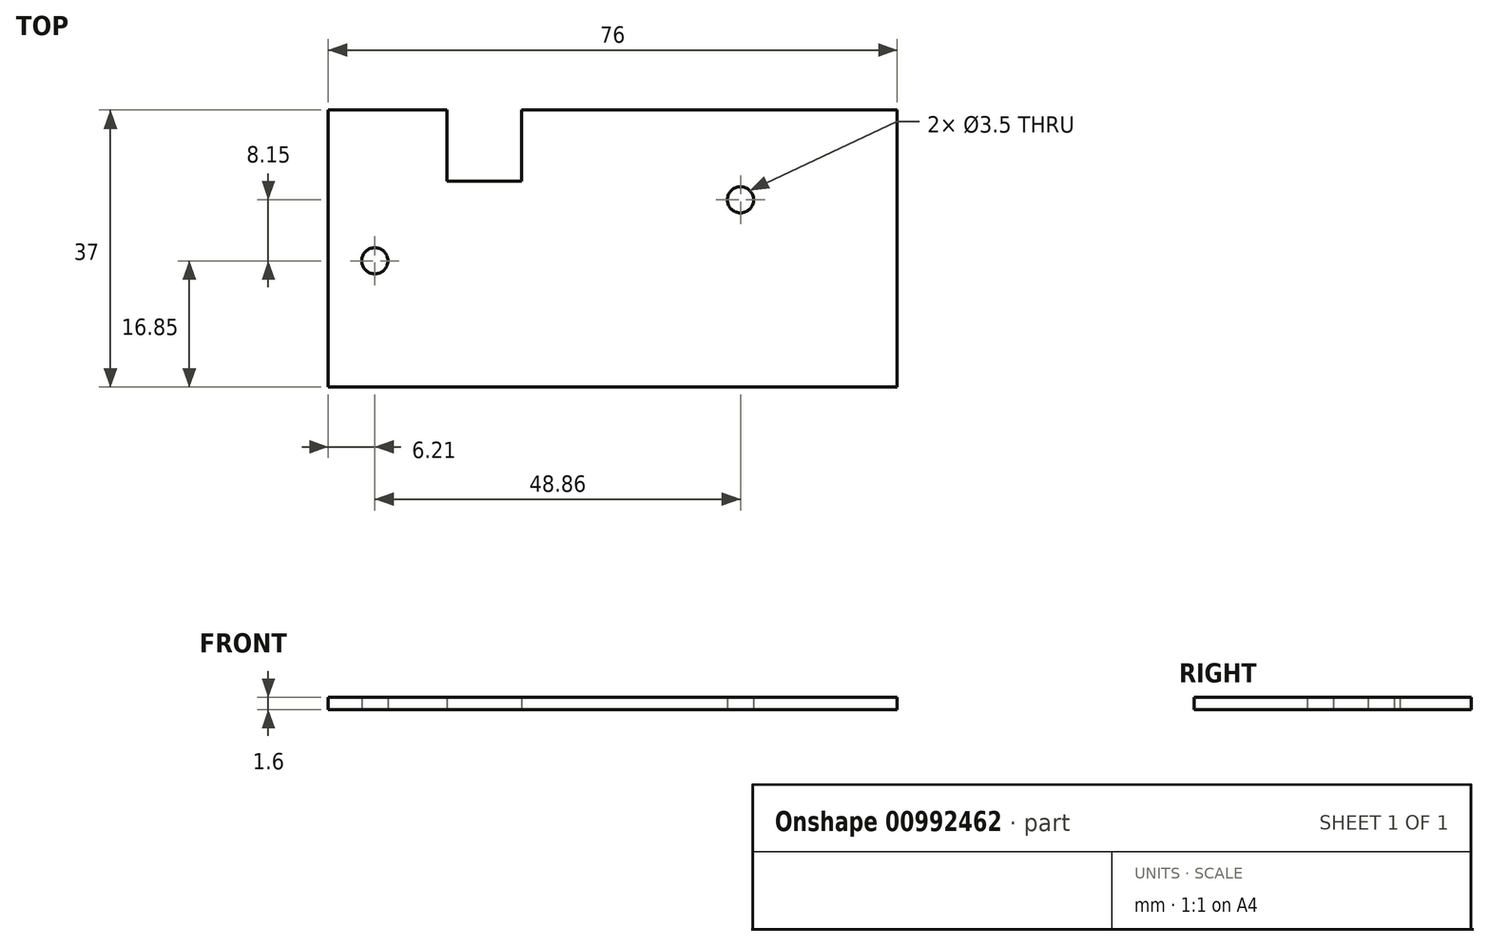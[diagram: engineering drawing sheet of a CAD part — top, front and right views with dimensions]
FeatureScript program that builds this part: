
annotation { "Feature Type Name" : "Feature", "Feature Type Description" : "" }
export const myFeature = defineFeature(function(context is Context, id is Id, definition is map)
    precondition{}
    {
        {
            var Q0;
            Q0=qCreatedBy(makeId("Top.planeOp"),FACE);
            var sketch = newSketch(context, id + "F0", { "sketchPlane" : qUnion([Q0])});
            skLineSegment(sketch, "E0.bottom", {"start": v(-38, 18.5) * mm, "end": v(-22.17, 18.5) * mm});
            skLineSegment(sketch, "E0.top", {"start": v(-38, -18.5) * mm, "end": v(38, -18.5) * mm});
            skLineSegment(sketch, "E0.left", {"start": v(-38, 18.5) * mm, "end": v(-38, -18.5) * mm});
            skLineSegment(sketch, "E0.right", {"start": v(38, 18.5) * mm, "end": v(38, -18.5) * mm});
            skLineSegment(sketch, "E1.top", {"start": v(-22.17, 9) * mm, "end": v(-12.17, 9) * mm});
            skLineSegment(sketch, "E1.left", {"start": v(-22.17, 18.5) * mm, "end": v(-22.17, 9) * mm});
            skLineSegment(sketch, "E1.right", {"start": v(-12.17, 18.5) * mm, "end": v(-12.17, 9) * mm});
            skLineSegment(sketch, "E2.trimOffspring", {"start": v(-12.17, 18.5) * mm, "end": v(38, 18.5) * mm});
            skCircle(sketch, "E3", {"center": v(-31.79, -1.65) * mm, "radius": 1.75 * mm});
            skCircle(sketch, "E4", {"center": v(17.07, 6.5) * mm, "radius": 1.75 * mm});
            skSolve(sketch);
        }
        {
            var Q0;
            Q0=makeQuery(id+"F0.imprint","IMPRINT",FACE,{"disambiguationData":[TD([[makeQuery(id+"F0.imprint","IMPRINT",EDGE,{"derivedFrom":sQuery(id+"F0.wireOp",EDGE,"E0.bottom")}),-1.0]])]});
            extrude(context, id + "F1", {"entities" : qUnion([Q0]), "depth" : 1.6 * mm, "offsetDistance" : 25 * mm});
        }
    });
